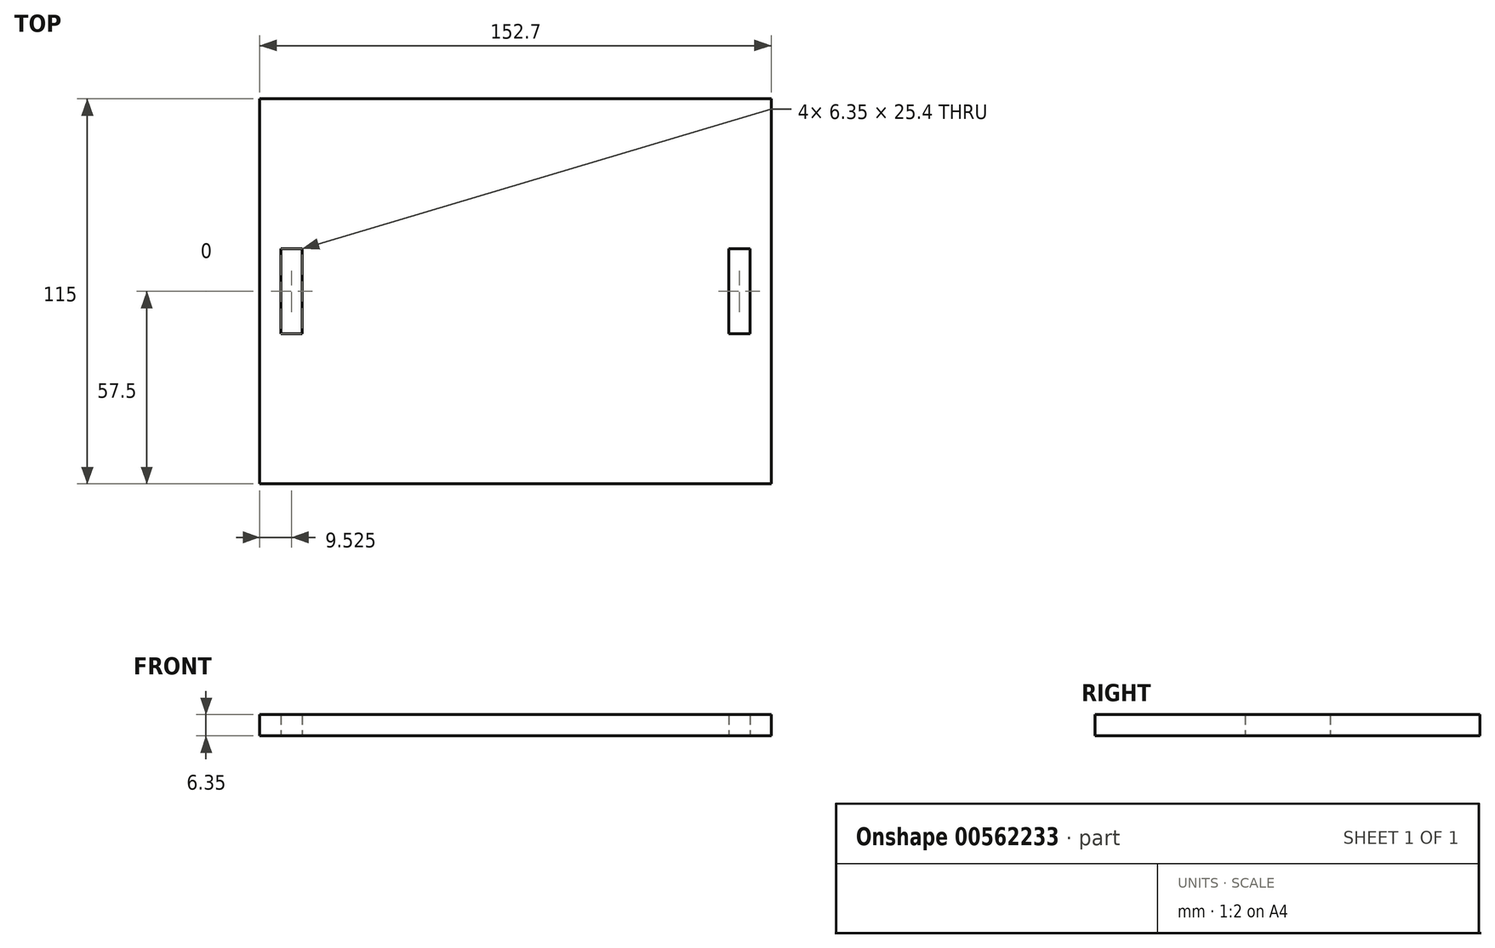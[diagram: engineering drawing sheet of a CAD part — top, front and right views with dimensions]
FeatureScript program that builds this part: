
annotation { "Feature Type Name" : "Feature", "Feature Type Description" : "" }
export const myFeature = defineFeature(function(context is Context, id is Id, definition is map)
    precondition{}
    {
        {
            var Q0;
            Q0=qCreatedBy(makeId("Top.planeOp"),FACE);
            var sketch = newSketch(context, id + "F0", { "sketchPlane" : qUnion([Q0])});
            skLineSegment(sketch, "E0.bottom", {"start": v(70, 57.5) * mm, "end": v(-70, 57.5) * mm});
            skLineSegment(sketch, "E0.top", {"start": v(70, -57.5) * mm, "end": v(-70, -57.5) * mm});
            skLineSegment(sketch, "E0.left", {"start": v(70, 57.5) * mm, "end": v(70, 12.7) * mm});
            skLineSegment(sketch, "E0.right", {"start": v(-70, 57.5) * mm, "end": v(-70, 12.7) * mm});
            skPoint(sketch, "E0.middle", {"position": v(0, 0) * mm});
            skLineSegment(sketch, "E1", {"start": v(-70, 12.7) * mm, "end": v(-63.65, 12.7) * mm});
            skLineSegment(sketch, "E2", {"start": v(-63.65, 12.7) * mm, "end": v(-63.65, -12.7) * mm});
            skLineSegment(sketch, "E3", {"start": v(-63.65, -12.7) * mm, "end": v(-70, -12.7) * mm});
            skLineSegment(sketch, "E4", {"start": v(70, 12.7) * mm, "end": v(63.65, 12.7) * mm});
            skLineSegment(sketch, "E5", {"start": v(63.65, 12.7) * mm, "end": v(63.65, -12.7) * mm});
            skLineSegment(sketch, "E6", {"start": v(63.65, -12.7) * mm, "end": v(70, -12.7) * mm});
            skLineSegment(sketch, "E7.trimOffspring", {"start": v(-70, -12.7) * mm, "end": v(-70, -57.5) * mm});
            skLineSegment(sketch, "E8.trimOffspring", {"start": v(70, -12.7) * mm, "end": v(70, -57.5) * mm});
            skLineSegment(sketch, "E9", {"start": v(-70, 57.5) * mm, "end": v(-76.35, 57.5) * mm});
            skLineSegment(sketch, "E10", {"start": v(-76.35, 57.5) * mm, "end": v(-76.35, -57.5) * mm});
            skLineSegment(sketch, "E11", {"start": v(-76.35, -57.5) * mm, "end": v(-70, -57.5) * mm});
            skLineSegment(sketch, "E12", {"start": v(70, 57.5) * mm, "end": v(76.35, 57.5) * mm});
            skLineSegment(sketch, "E13", {"start": v(76.35, 57.5) * mm, "end": v(76.35, -57.5) * mm});
            skLineSegment(sketch, "E14", {"start": v(76.35, -57.5) * mm, "end": v(70, -57.5) * mm});
            skLineSegment(sketch, "E15", {"start": v(-70, 12.7) * mm, "end": v(-70, -12.7) * mm});
            skLineSegment(sketch, "E16", {"start": v(70, 12.7) * mm, "end": v(70, -12.7) * mm});
            skSolve(sketch);
        }
        {
            var Q0;
            Q0 = qSketchRegion(id + "F0", true);
            extrude(context, id + "F1", {"entities" : qUnion([Q0]), "depth" : 6.35 * mm, "offsetDistance" : 25.4 * mm});
        }
    });
